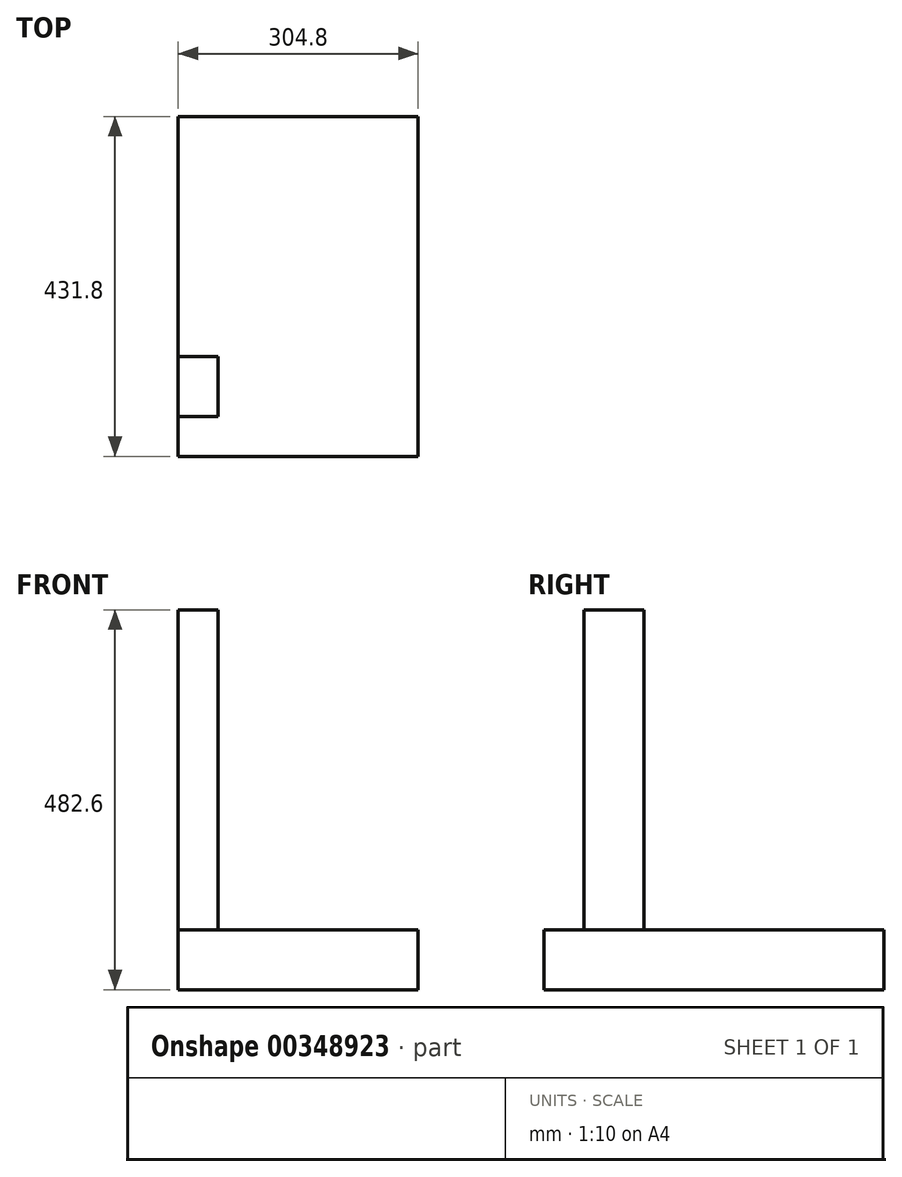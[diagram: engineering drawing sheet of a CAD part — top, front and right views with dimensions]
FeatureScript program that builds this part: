
annotation { "Feature Type Name" : "Feature", "Feature Type Description" : "" }
export const myFeature = defineFeature(function(context is Context, id is Id, definition is map)
    precondition{}
    {
        {
            var Q0;
            Q0=qCreatedBy(makeId("Front.planeOp"),FACE);
            var sketch = newSketch(context, id + "F0", { "sketchPlane" : qUnion([Q0])});
            skLineSegment(sketch, "E0.bottom", {"start": v(-152.4, -38.1) * mm, "end": v(152.4, -38.1) * mm});
            skLineSegment(sketch, "E0.top", {"start": v(-101.6, 38.1) * mm, "end": v(152.4, 38.1) * mm});
            skLineSegment(sketch, "E0.left", {"start": v(-152.4, -38.1) * mm, "end": v(-152.4, 38.1) * mm});
            skLineSegment(sketch, "E0.right", {"start": v(152.4, -38.1) * mm, "end": v(152.4, 38.1) * mm});
            skPoint(sketch, "E0.middle", {"position": v(0, 0) * mm});
            skLineSegment(sketch, "E1.top", {"start": v(-152.4, 444.5) * mm, "end": v(-101.6, 444.5) * mm});
            skLineSegment(sketch, "E1.left", {"start": v(-152.4, 38.1) * mm, "end": v(-152.4, 444.5) * mm});
            skLineSegment(sketch, "E1.right", {"start": v(-101.6, 38.1) * mm, "end": v(-101.6, 444.5) * mm});
            skPoint(sketch, "E1.middle", {"position": v(-127, 241.3) * mm});
            skSolve(sketch);
        }
        {
            var Q0;
            Q0 = qSketchRegion(id + "F0", true);
            extrude(context, id + "F1", {"entities" : qUnion([Q0]), "depth" : 76.2 * mm});
        }
        {
            var Q0;
            Q0=makeQuery(id+"F1.opExtrude","CAP_FACE",FACE,{"disambiguationData":[OSD([sQuery(id+"F0.wireOp",EDGE,"E0.bottom"),sQuery(id+"F0.wireOp",EDGE,"E0.top"),sQuery(id+"F0.wireOp",EDGE,"E0.left"),sQuery(id+"F0.wireOp",EDGE,"E0.right"),sQuery(id+"F0.wireOp",EDGE,"E1.top"),sQuery(id+"F0.wireOp",EDGE,"E1.left"),sQuery(id+"F0.wireOp",EDGE,"E1.right")])],"isStart":true});
            var sketch = newSketch(context, id + "F2", { "sketchPlane" : qUnion([Q0])});
            skLineSegment(sketch, "E2.bottom", {"start": v(-152.4, 38.1) * mm, "end": v(152.4, 38.1) * mm});
            skLineSegment(sketch, "E2.top", {"start": v(-152.4, -38.1) * mm, "end": v(152.4, -38.1) * mm});
            skLineSegment(sketch, "E2.left", {"start": v(-152.4, 38.1) * mm, "end": v(-152.4, -38.1) * mm});
            skLineSegment(sketch, "E2.right", {"start": v(152.4, 38.1) * mm, "end": v(152.4, -38.1) * mm});
            skSolve(sketch);
        }
        {
            var Q0;
            Q0 = qSketchRegion(id + "F2", true);
            extrude(context, id + "F3", {"entities" : qUnion([Q0]), "operationType" : NewBodyOperationType.ADD, "depth" : 304.8 * mm, "hasSecondDirection" : true, "secondDirectionOppositeDirection" : true, "secondDirectionDepth" : 127 * mm});
        }
    });
